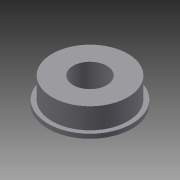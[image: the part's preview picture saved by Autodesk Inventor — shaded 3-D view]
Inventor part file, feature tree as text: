
AUTODESK INVENTOR PART (.ipt)
format: ipt  version: 2015 (Build 190159000, 159)  size: 86,528 bytes
history: native  units: in
note: dims shown in document units (in); Inventor stores cm internally (conversion verified against a paired STEP export)
features: extrude x2, sketch x1
ambient origin geometry x8: Origin, YZ Plane, XZ Plane, XY Plane, X Axis, Y Axis, Z Axis, Center Point
bodies: Solid1 (feature_tree)
feature tree (3):
  sketch  "Sketch1"  dims[d0=1.125in d1=1.25in d2=0.5in d3=0.375in d4=0.0in d5=0.065in d6=0.0in]
  extrude  "Extrusion1"  Depth=0.065in
  extrude  "Extrusion2"  Depth=0.065in
